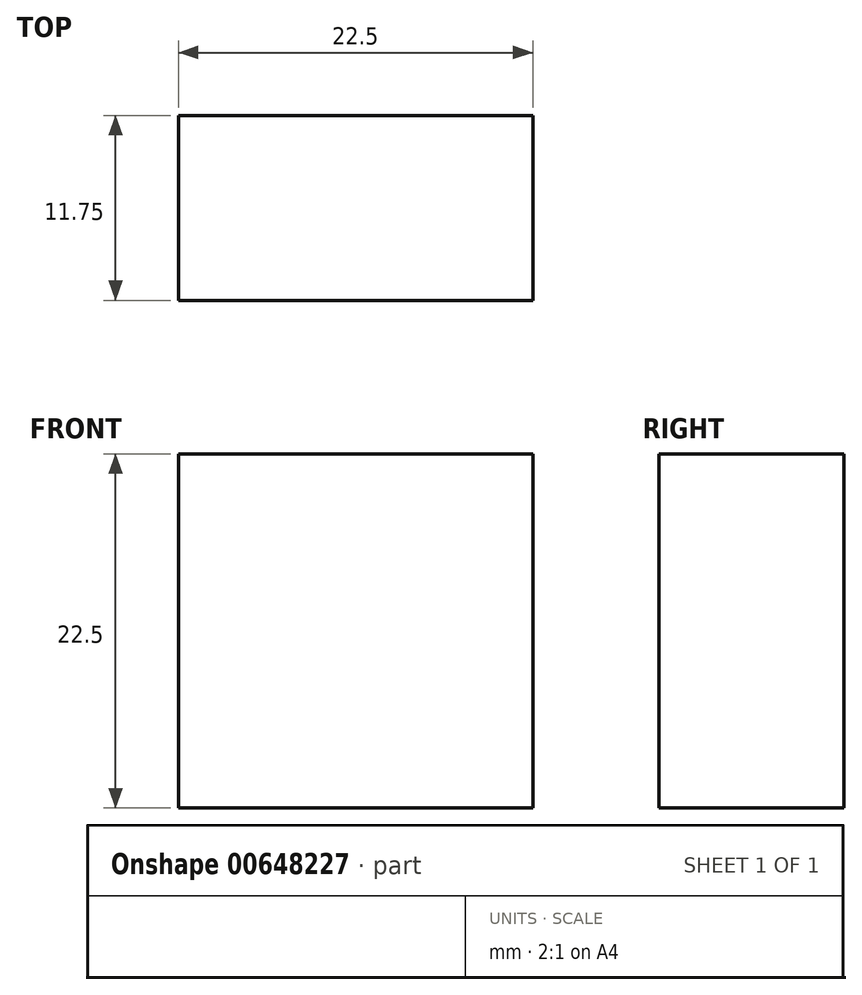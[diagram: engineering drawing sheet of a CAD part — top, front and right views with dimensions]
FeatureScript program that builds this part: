
annotation { "Feature Type Name" : "Feature", "Feature Type Description" : "" }
export const myFeature = defineFeature(function(context is Context, id is Id, definition is map)
    precondition{}
    {
        {
            var Q0;
            Q0=qCreatedBy(makeId("Top.planeOp"),FACE);
            var sketch = newSketch(context, id + "F0", { "sketchPlane" : qUnion([Q0])});
            skLineSegment(sketch, "E0.bottom", {"start": v(0, 0) * mm, "end": v(22.5, 0) * mm});
            skLineSegment(sketch, "E0.top", {"start": v(0, -11.75) * mm, "end": v(22.5, -11.75) * mm});
            skLineSegment(sketch, "E0.left", {"start": v(0, 0) * mm, "end": v(0, -11.75) * mm});
            skLineSegment(sketch, "E0.right", {"start": v(22.5, 0) * mm, "end": v(22.5, -11.75) * mm});
            skSolve(sketch);
        }
        {
            var Q0;
            Q0 = qSketchRegion(id + "F0", true);
            extrude(context, id + "F1", {"entities" : qUnion([Q0]), "oppositeDirection" : true, "depth" : 22.5 * mm, "offsetDistance" : 25 * mm});
        }
    });
